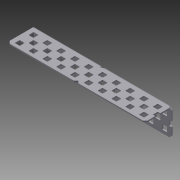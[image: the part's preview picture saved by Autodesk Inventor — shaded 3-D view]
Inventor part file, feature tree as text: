
AUTODESK INVENTOR PART (.ipt)
format: ipt  version: 2012 (Build 160160000, 160)  size: 1,193,984 bytes
history: native  units: in
note: dims shown in document units (in); Inventor stores cm internally (conversion verified against a paired STEP export)
features: sketch x2, other x1, imported_body x1, plane x1, split x1
ambient origin geometry x8: Origin, YZ Plane, XZ Plane, XY Plane, X Axis, Y Axis, Z Axis, Center Point
feature tree (6):
  parser-record x1  (decoder bookkeeping rows leaked as tree rows — omitted from the tree; the rows remain in map.json)
  imported_body  "Base1"
  sketch  "Sketch5"  dims[d18=5.9055in d20=0.5in d21=0.7874in d23=0.5in]
  sketch  "Sketch6"  dims[d26=5.5118in d28=0.5in d29=0.3937in d31=1.0in d33=0.5in d34=0.5in d35=0.5in d41=-2.5in]
  plane  "Work Plane1"
  split  "Split1"
